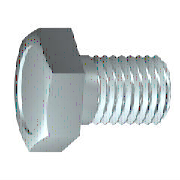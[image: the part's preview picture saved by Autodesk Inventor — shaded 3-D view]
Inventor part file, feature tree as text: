
AUTODESK INVENTOR PART (.ipt)
format: ipt  version: 2021 (Build 250183000, 183)  size: 201,728 bytes
history: native  units: mm (DEFAULTED — no unit token found)
features: sketch x4, extrude x2, chamfer x1, plane x1
ambient origin geometry x7: Origin, YZ Plane, XY Plane, X Axis, Y Axis, Z Axis, Center Point
bodies: Solid1 (feature_tree), Body (feature_tree)
feature tree (8):
  extrude  "Head"  Depth=40.0mm
  extrude  "Indent1"  Depth=13.0mm
  chamfer  "Chamfer1"  Angle=30.0deg  [1 undecoded]
  plane  "Work Plane1"
  sketch  "Sketch1"  dims[d0=8.0mm d1=40.0mm]
  sketch  "Sketch2"  dims[d5=90.0deg d2=13.0mm]
  sketch  "Sketch4"  dims[d4=0.0mm d6=30.0deg d7=30.0deg d13=90.0deg d8=37.5mm d9=0.0mm d11=0.4mm d12=9.75mm d14=1.3mm d15=0.0mm d16=13.0mm d17=13.0mm d18=15.011107mm d20=0.0mm d33=0.0mm d34=0.0mm]
  sketch  "Sketch3"  dims[d3=6.5mm]
note: 1 required parameter value undecoded (feature->parameter linkage not recoverable at this tier; creation-order binding heuristic only, values carry confidence <= 0.55)
